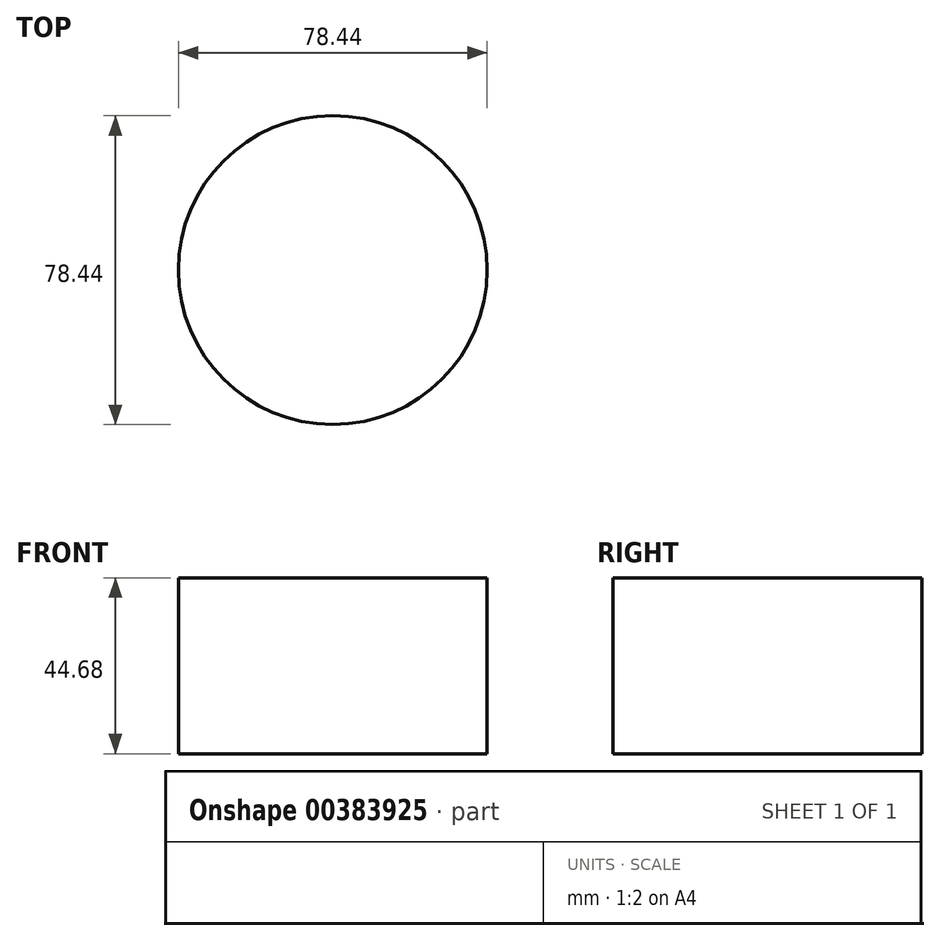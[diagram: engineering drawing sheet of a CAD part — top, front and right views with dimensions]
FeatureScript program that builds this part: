
annotation { "Feature Type Name" : "Feature", "Feature Type Description" : "" }
export const myFeature = defineFeature(function(context is Context, id is Id, definition is map)
    precondition{}
    {
        {
            var Q0;
            Q0=qCreatedBy(makeId("Front.planeOp"),FACE);
            var sketch = newSketch(context, id + "F0", { "sketchPlane" : qUnion([Q0])});
            skLineSegment(sketch, "E0.bottom", {"start": v(19.61, 22.34) * mm, "end": v(-19.61, 22.34) * mm});
            skLineSegment(sketch, "E0.top", {"start": v(19.61, -22.34) * mm, "end": v(-19.61, -22.34) * mm});
            skLineSegment(sketch, "E0.left", {"start": v(19.61, 22.34) * mm, "end": v(19.61, -22.34) * mm});
            skLineSegment(sketch, "E0.right", {"start": v(-19.61, 22.34) * mm, "end": v(-19.61, -22.34) * mm});
            skPoint(sketch, "E0.middle", {"position": v(0, 0) * mm});
            skPoint(sketch, "E1", {"position": v(19.61, 7.78) * mm});
            skPoint(sketch, "E2", {"position": v(14.64, 3.54) * mm});
            skPoint(sketch, "E3", {"position": v(19.61, 0) * mm});
            skSolve(sketch);
        }
        {
            var Q0;
            Q0=makeQuery(id+"F0.imprint","IMPRINT",FACE,{"disambiguationData":[TD([[makeQuery(id+"F0.imprint","IMPRINT",EDGE,{"derivedFrom":sQuery(id+"F0.wireOp",EDGE,"E0.bottom")}),1.0]])]});
            var Q1;
            Q1=sQuery(id+"F0.wireOp",EDGE,"E0.right");
            revolve(context, id + "F1", {"entities" : qUnion([Q0]), "axis" : qUnion([Q1]), "revolveType" : RevolveType.FULL});
        }
    });
